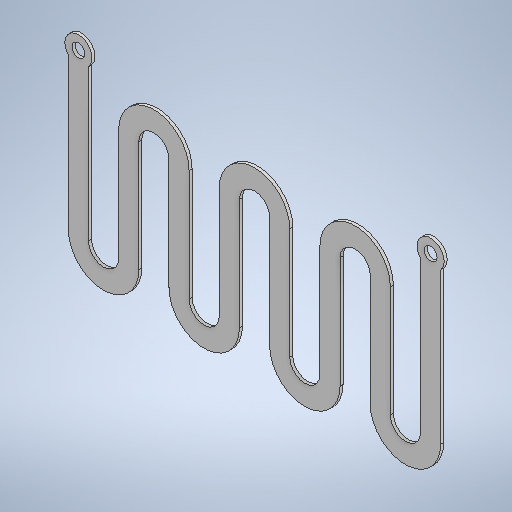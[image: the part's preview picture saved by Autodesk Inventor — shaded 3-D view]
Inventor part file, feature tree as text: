
AUTODESK INVENTOR PART (.ipt)
format: ipt  version: 2025.2 (Build 292293000, 293)  size: 335,360 bytes
history: native  units: mm
features: other x1, extrude x1, sketch x1
ambient origin geometry x8: Origin, YZ Plane, XZ Plane, XY Plane, X Axis, Y Axis, Z Axis, Center Point
bodies: Body1 (feature_tree)
feature tree (3):
  other  "Sólido1"
  extrude  "Extrusão1"  Depth=300.0mm
  sketch  "Esboço1"  dims[d0=10000.0mm d1=17500.0mm d2=2700.0mm d5=15000.0mm d7=3000.0mm d8=2000.0mm d12=1300.0mm d13=300.0mm d14=0.0mm]
